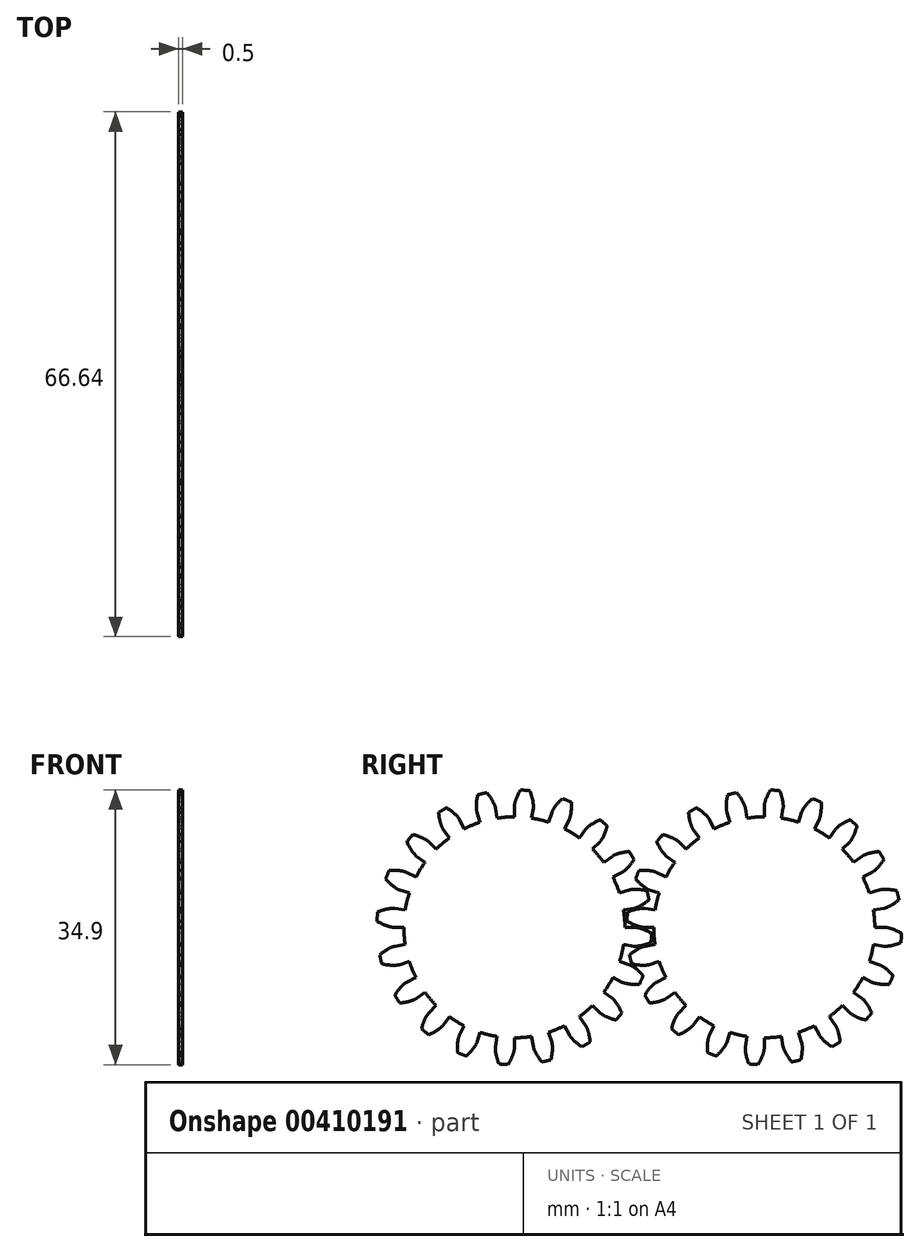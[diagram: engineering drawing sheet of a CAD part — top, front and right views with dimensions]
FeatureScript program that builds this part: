
annotation { "Feature Type Name" : "Feature", "Feature Type Description" : "" }
export const myFeature = defineFeature(function(context is Context, id is Id, definition is map)
    precondition{}
    {
        {
            assignVariable(context, id + "F0", {"name" : "NumberTeeth", "anyValue" : 20});
        }
        {
            assignVariable(context, id + "F1", {"name" : "GearThickness", "anyValue" : .5});
        }
        {
            var Q0;
            Q0=qCreatedBy(makeId("Right.planeOp"),FACE);
            var sketch = newSketch(context, id + "F2", { "sketchPlane" : qUnion([Q0])});
            skCircle(sketch, "E0", {"center": v(0, 0) * mm, "radius": 14.04 * mm});
            skCircle(sketch, "E1", {"center": v(0, 0) * mm, "radius": 15.37 * mm, "construction": true});
            skCircle(sketch, "E2", {"center": v(0, 0) * mm, "radius": 15.88 * mm, "construction": true});
            skCircle(sketch, "E3", {"center": v(0, 0) * mm, "radius": 17.46 * mm});
            skLineSegment(sketch, "E4", {"start": v(0, 0) * mm, "end": v(-15.37, 0) * mm, "construction": true});
            skLineSegment(sketch, "E5.1.0", {"start": v(0, 0) * mm, "end": v(-15.35, 0.77) * mm, "construction": true});
            skLineSegment(sketch, "E5.2.0", {"start": v(0, 0) * mm, "end": v(-15.3, 1.53) * mm, "construction": true});
            skLineSegment(sketch, "E5.3.0", {"start": v(0, 0) * mm, "end": v(-15.2, 2.3) * mm, "construction": true});
            skLineSegment(sketch, "E5.4.0", {"start": v(0, 0) * mm, "end": v(-15.06, 3.05) * mm, "construction": true});
            skLineSegment(sketch, "E5.5.0", {"start": v(0, 0) * mm, "end": v(-14.9, 3.8) * mm, "construction": true});
            skLineSegment(sketch, "E5.6.0", {"start": v(0, 0) * mm, "end": v(-14.68, 4.54) * mm, "construction": true});
            skLineSegment(sketch, "E5.7.0", {"start": v(0, 0) * mm, "end": v(-14.44, 5.27) * mm, "construction": true});
            skLineSegment(sketch, "E5.8.0", {"start": v(0, 0) * mm, "end": v(-14.16, 5.99) * mm, "construction": true});
            skLineSegment(sketch, "E5.9.0", {"start": v(0, 0) * mm, "end": v(-13.84, 6.69) * mm, "construction": true});
            skLineSegment(sketch, "E5.10.0", {"start": v(0, 0) * mm, "end": v(-13.49, 7.37) * mm, "construction": true});
            skLineSegment(sketch, "E5.11.0", {"start": v(0, 0) * mm, "end": v(-13.1, 8.03) * mm, "construction": true});
            skLineSegment(sketch, "E5.12.0", {"start": v(0, 0) * mm, "end": v(-12.68, 8.68) * mm, "construction": true});
            skLineSegment(sketch, "E5.13.0", {"start": v(0, 0) * mm, "end": v(-12.24, 9.3) * mm, "construction": true});
            skLineSegment(sketch, "E5.14.0", {"start": v(0, 0) * mm, "end": v(-11.76, 9.9) * mm, "construction": true});
            skLineSegment(sketch, "E5.anchor2", {"start": v(0, 0) * mm, "end": v(-11.76, 9.9) * mm, "construction": true});
            skLineSegment(sketch, "E6", {"start": v(-15.35, 0.77) * mm, "end": v(-15.39, 0) * mm, "construction": true});
            skLineSegment(sketch, "E7", {"start": v(-15.3, 1.53) * mm, "end": v(-15.45, 0) * mm, "construction": true});
            skLineSegment(sketch, "E8", {"start": v(-15.2, 2.3) * mm, "end": v(-15.54, 0.02) * mm, "construction": true});
            skLineSegment(sketch, "E9", {"start": v(-14.9, 3.8) * mm, "end": v(-15.84, 0.08) * mm, "construction": true});
            skLineSegment(sketch, "E10", {"start": v(-14.68, 4.54) * mm, "end": v(-16.05, 0.14) * mm, "construction": true});
            skLineSegment(sketch, "E11", {"start": v(-14.44, 5.27) * mm, "end": v(-16.28, 0.22) * mm, "construction": true});
            skLineSegment(sketch, "E12", {"start": v(-14.16, 5.99) * mm, "end": v(-16.55, 0.32) * mm, "construction": true});
            skLineSegment(sketch, "E13", {"start": v(-13.84, 6.69) * mm, "end": v(-16.85, 0.46) * mm, "construction": true});
            skLineSegment(sketch, "E14", {"start": v(-13.49, 7.37) * mm, "end": v(-17.17, 0.62) * mm, "construction": true});
            skLineSegment(sketch, "E15", {"start": v(-13.1, 8.03) * mm, "end": v(-17.52, 0.83) * mm, "construction": true});
            skLineSegment(sketch, "E16", {"start": v(-15.06, 3.05) * mm, "end": v(-15.67, 0.04) * mm, "construction": true});
            skLineSegment(sketch, "E17", {"start": v(-12.68, 8.68) * mm, "end": v(-17.9, 1.07) * mm, "construction": true});
            skLineSegment(sketch, "E18", {"start": v(-12.24, 9.3) * mm, "end": v(-18.28, 1.35) * mm, "construction": true});
            skLineSegment(sketch, "E19", {"start": v(-11.76, 9.9) * mm, "end": v(-18.69, 1.67) * mm, "construction": true});
            skLineSegment(sketch, "E20", {"start": v(0, 0) * mm, "end": v(-15.32, 1.2) * mm, "construction": true});
            skLineSegment(sketch, "E21", {"start": v(-14.04, 0) * mm, "end": v(-15.37, 0) * mm});
            skLineSegment(sketch, "E22.MirrorCS", {"start": v(-13.87, 2.2) * mm, "end": v(-15.18, 2.4) * mm});
            skFitSpline(sketch, "E23", {"points": [v(-15.37, 0) * mm, v(-15.39, 0) * mm, v(-15.45, 0) * mm, v(-15.54, 0.02) * mm, v(-15.67, 0.04) * mm, v(-15.84, 0.08) * mm, v(-16.05, 0.14) * mm, v(-16.28, 0.22) * mm, v(-16.55, 0.32) * mm, v(-16.85, 0.46) * mm, v(-17.17, 0.62) * mm, v(-17.52, 0.83) * mm, v(-17.9, 1.07) * mm, v(-18.28, 1.35) * mm, v(-18.69, 1.67) * mm], "startDerivative": vector(-0.82, 0) * mm, "endDerivative": vector(-1.2, 1) * mm});
            skLineSegment(sketch, "E24", {"start": v(-18.69, 1.67) * mm, "end": v(-19.04, 1.97) * mm, "construction": true});
            skFitSpline(sketch, "E25.MirrorCS", {"points": [v(-15.18, 2.4) * mm, v(-15.2, 2.4) * mm, v(-15.26, 2.41) * mm, v(-15.35, 2.41) * mm, v(-15.49, 2.41) * mm, v(-15.66, 2.4) * mm, v(-15.87, 2.37) * mm, v(-16.12, 2.33) * mm, v(-16.4, 2.27) * mm, v(-16.71, 2.18) * mm, v(-17.06, 2.07) * mm, v(-17.43, 1.92) * mm, v(-17.84, 1.74) * mm, v(-18.27, 1.53) * mm, v(-18.72, 1.27) * mm], "startDerivative": vector(-0.8, 0.13) * mm, "endDerivative": vector(-1.34, -0.8) * mm});
            skSolve(sketch);
        }
        {
            var Q0;
            {var subQ0=sQuery(id+"F2.wireOp",EDGE,"E0");var subQ27=makeQuery(id+"F2.imprint","INTERSECT",VERTEX,{"derivedFrom":[subQ0,sQuery(id+"F2.wireOp",EDGE,"10ea1024-8cf5-41f5-a75f-a634b86921f3.10.0")]});Q0=makeQuery(id+"F2.imprint","IMPRINT",FACE,{"disambiguationData":[TD([[makeQuery(id+"F2.imprint","IMPRINT",EDGE,{"disambiguationData":[TD([[subQ27,-1.0]])],"derivedFrom":subQ0}),1.0]])]});}
            var Q1;
            {var subQ0=sQuery(id+"F2.wireOp",EDGE,"10ea1024-8cf5-41f5-a75f-a634b86921f3.1.0");Q1=makeQuery(id+"F2.imprint","IMPRINT",FACE,{"disambiguationData":[TD([[makeQuery(id+"F2.imprint","IMPRINT",EDGE,{"derivedFrom":subQ0}),-1.0]])]});}
            var Q2;
            {var subQ7=sQuery(id+"F2.wireOp",EDGE,"10ea1024-8cf5-41f5-a75f-a634b86921f3.2.0");Q2=makeQuery(id+"F2.imprint","IMPRINT",FACE,{"disambiguationData":[TD([[makeQuery(id+"F2.imprint","IMPRINT",EDGE,{"derivedFrom":subQ7}),-1.0]])]});}
            var Q3;
            {var subQ8=sQuery(id+"F2.wireOp",EDGE,"10ea1024-8cf5-41f5-a75f-a634b86921f3.3.0");Q3=makeQuery(id+"F2.imprint","IMPRINT",FACE,{"disambiguationData":[TD([[makeQuery(id+"F2.imprint","IMPRINT",EDGE,{"derivedFrom":subQ8}),-1.0]])]});}
            var Q4;
            {var subQ2=sQuery(id+"F2.wireOp",EDGE,"10ea1024-8cf5-41f5-a75f-a634b86921f3.4.0");Q4=makeQuery(id+"F2.imprint","IMPRINT",FACE,{"disambiguationData":[TD([[makeQuery(id+"F2.imprint","IMPRINT",EDGE,{"derivedFrom":subQ2}),-1.0]])]});}
            var Q5;
            {var subQ8=sQuery(id+"F2.wireOp",EDGE,"10ea1024-8cf5-41f5-a75f-a634b86921f3.5.0");Q5=makeQuery(id+"F2.imprint","IMPRINT",FACE,{"disambiguationData":[TD([[makeQuery(id+"F2.imprint","IMPRINT",EDGE,{"derivedFrom":subQ8}),-1.0]])]});}
            var Q6;
            {var subQ3=sQuery(id+"F2.wireOp",EDGE,"10ea1024-8cf5-41f5-a75f-a634b86921f3.6.0");Q6=makeQuery(id+"F2.imprint","IMPRINT",FACE,{"disambiguationData":[TD([[makeQuery(id+"F2.imprint","IMPRINT",EDGE,{"derivedFrom":subQ3}),-1.0]])]});}
            var Q7;
            {var subQ0=sQuery(id+"F2.wireOp",EDGE,"10ea1024-8cf5-41f5-a75f-a634b86921f3.7.0");Q7=makeQuery(id+"F2.imprint","IMPRINT",FACE,{"disambiguationData":[TD([[makeQuery(id+"F2.imprint","IMPRINT",EDGE,{"derivedFrom":subQ0}),-1.0]])]});}
            var Q8;
            {var subQ5=sQuery(id+"F2.wireOp",EDGE,"10ea1024-8cf5-41f5-a75f-a634b86921f3.8.0");Q8=makeQuery(id+"F2.imprint","IMPRINT",FACE,{"disambiguationData":[TD([[makeQuery(id+"F2.imprint","IMPRINT",EDGE,{"derivedFrom":subQ5}),-1.0]])]});}
            var Q9;
            {var subQ1=sQuery(id+"F2.wireOp",EDGE,"10ea1024-8cf5-41f5-a75f-a634b86921f3.9.0");Q9=makeQuery(id+"F2.imprint","IMPRINT",FACE,{"disambiguationData":[TD([[makeQuery(id+"F2.imprint","IMPRINT",EDGE,{"derivedFrom":subQ1}),-1.0]])]});}
            var Q10;
            {var subQ5=sQuery(id+"F2.wireOp",EDGE,"10ea1024-8cf5-41f5-a75f-a634b86921f3.10.0");Q10=makeQuery(id+"F2.imprint","IMPRINT",FACE,{"disambiguationData":[TD([[makeQuery(id+"F2.imprint","IMPRINT",EDGE,{"derivedFrom":subQ5}),-1.0]])]});}
            var Q11;
            {var subQ8=sQuery(id+"F2.wireOp",EDGE,"10ea1024-8cf5-41f5-a75f-a634b86921f3.11.0");Q11=makeQuery(id+"F2.imprint","IMPRINT",FACE,{"disambiguationData":[TD([[makeQuery(id+"F2.imprint","IMPRINT",EDGE,{"derivedFrom":subQ8}),-1.0]])]});}
            var Q12;
            {var subQ2=sQuery(id+"F2.wireOp",EDGE,"10ea1024-8cf5-41f5-a75f-a634b86921f3.12.0");Q12=makeQuery(id+"F2.imprint","IMPRINT",FACE,{"disambiguationData":[TD([[makeQuery(id+"F2.imprint","IMPRINT",EDGE,{"derivedFrom":subQ2}),-1.0]])]});}
            var Q13;
            {var subQ3=sQuery(id+"F2.wireOp",EDGE,"10ea1024-8cf5-41f5-a75f-a634b86921f3.13.0");Q13=makeQuery(id+"F2.imprint","IMPRINT",FACE,{"disambiguationData":[TD([[makeQuery(id+"F2.imprint","IMPRINT",EDGE,{"derivedFrom":subQ3}),-1.0]])]});}
            var Q14;
            {var subQ0=sQuery(id+"F2.wireOp",EDGE,"10ea1024-8cf5-41f5-a75f-a634b86921f3.14.0");Q14=makeQuery(id+"F2.imprint","IMPRINT",FACE,{"disambiguationData":[TD([[makeQuery(id+"F2.imprint","IMPRINT",EDGE,{"derivedFrom":subQ0}),-1.0]])]});}
            var Q15;
            {var subQ6=sQuery(id+"F2.wireOp",EDGE,"10ea1024-8cf5-41f5-a75f-a634b86921f3.15.0");Q15=makeQuery(id+"F2.imprint","IMPRINT",FACE,{"disambiguationData":[TD([[makeQuery(id+"F2.imprint","IMPRINT",EDGE,{"derivedFrom":subQ6}),-1.0]])]});}
            var Q16;
            {var subQ5=sQuery(id+"F2.wireOp",EDGE,"10ea1024-8cf5-41f5-a75f-a634b86921f3.16.0");Q16=makeQuery(id+"F2.imprint","IMPRINT",FACE,{"disambiguationData":[TD([[makeQuery(id+"F2.imprint","IMPRINT",EDGE,{"derivedFrom":subQ5}),-1.0]])]});}
            var Q17;
            {var subQ7=sQuery(id+"F2.wireOp",EDGE,"10ea1024-8cf5-41f5-a75f-a634b86921f3.17.0");Q17=makeQuery(id+"F2.imprint","IMPRINT",FACE,{"disambiguationData":[TD([[makeQuery(id+"F2.imprint","IMPRINT",EDGE,{"derivedFrom":subQ7}),-1.0]])]});}
            var Q18;
            {var subQ5=sQuery(id+"F2.wireOp",EDGE,"10ea1024-8cf5-41f5-a75f-a634b86921f3.18.0");Q18=makeQuery(id+"F2.imprint","IMPRINT",FACE,{"disambiguationData":[TD([[makeQuery(id+"F2.imprint","IMPRINT",EDGE,{"derivedFrom":subQ5}),-1.0]])]});}
            var Q19;
            {var subQ8=sQuery(id+"F2.wireOp",EDGE,"10ea1024-8cf5-41f5-a75f-a634b86921f3.19.0");Q19=makeQuery(id+"F2.imprint","IMPRINT",FACE,{"disambiguationData":[TD([[makeQuery(id+"F2.imprint","IMPRINT",EDGE,{"derivedFrom":subQ8}),-1.0]])]});}
            var Q20;
            {var subQ8=sQuery(id+"F2.wireOp",EDGE,"E21");Q20=makeQuery(id+"F2.imprint","IMPRINT",FACE,{"disambiguationData":[TD([[makeQuery(id+"F2.imprint","IMPRINT",EDGE,{"derivedFrom":subQ8}),-1.0]])]});}
            extrude(context, id + "F3", {"entities" : qUnion([Q0, Q1, Q2, Q3, Q4, Q5, Q6, Q7, Q8, Q9, Q10, Q11, Q12, Q13, Q14, Q15, Q16, Q17, Q18, Q19, Q20]), "depth" : (getVariable(context, 'GearThickness')) * mm});
        }
        {
            var Q0;
            Q0=makeQuery(id+"F3.opExtrude","SWEPT_FACE",FACE,{"disambiguationData":[OSD([sQuery(id+"F2.wireOp",EDGE,"E25.MirrorCS")])]});
            var Q1;
            Q1=makeQuery(id+"F3.opExtrude","SWEPT_FACE",FACE,{"disambiguationData":[OSD([sQuery(id+"F2.wireOp",EDGE,"E23")])]});
            var Q2;
            Q2=makeQuery(id+"F3.opExtrude","SWEPT_FACE",FACE,{"disambiguationData":[OSD([sQuery(id+"F2.wireOp",EDGE,"E3")])]});
            var Q3;
            Q3=makeQuery(id+"F3.opExtrude","SWEPT_FACE",FACE,{"disambiguationData":[OSD([sQuery(id+"F2.wireOp",EDGE,"E22.MirrorCS")])]});
            var Q4;
            Q4=makeQuery(id+"F3.opExtrude","SWEPT_FACE",FACE,{"disambiguationData":[OSD([sQuery(id+"F2.wireOp",EDGE,"E21")])]});
            var Q5;
            Q5=makeQuery(id+"F3.opExtrude","SWEPT_FACE",FACE,{"disambiguationData":[OSD([sQuery(id+"F2.wireOp",EDGE,"E0")])]});
            circularPattern(context, id + "F4", {"faces" : qUnion([Q0, Q1, Q2, Q3, Q4]), "axis" : qUnion([Q5]), "angle" : 360 * degree, "instanceCount" : getVariable(context, 'NumberTeeth'), "equalSpace" : true, "patternType" : PatternType.FACE});
        }
        {
            var Q0;
            Q0=makeQuery(id+"F3.opExtrude","SWEPT_BODY",BODY,{"disambiguationData":[OSD([sQuery(id+"F2.wireOp",EDGE,"E0"),sQuery(id+"F2.wireOp",EDGE,"E3"),sQuery(id+"F2.wireOp",EDGE,"E21"),sQuery(id+"F2.wireOp",EDGE,"E22.MirrorCS"),sQuery(id+"F2.wireOp",EDGE,"E23"),sQuery(id+"F2.wireOp",EDGE,"E25.MirrorCS")])]});
            transform(context, id + "F5", {"entities" : qUnion([Q0]), "transformType" : TransformType.TRANSLATION_3D, "dx" : 0 * mm, "dy" : 33.33 * mm, "dz" : 0 * mm, "makeCopy" : true});
        }
        {
            var Q0;
            Q0=makeQuery(id+"F5.opPattern","COPY",BODY,{"derivedFrom":makeQuery(id+"F3.opExtrude","SWEPT_BODY",BODY,{"disambiguationData":[OSD([sQuery(id+"F2.wireOp",EDGE,"E0"),sQuery(id+"F2.wireOp",EDGE,"E3"),sQuery(id+"F2.wireOp",EDGE,"E21"),sQuery(id+"F2.wireOp",EDGE,"E22.MirrorCS"),sQuery(id+"F2.wireOp",EDGE,"E23"),sQuery(id+"F2.wireOp",EDGE,"E25.MirrorCS")])]}),"instanceName":"1"});
            transform(context, id + "F6", {"entities" : qUnion([Q0]), "transformType" : TransformType.TRANSLATION_3D, "dx" : 0 * mm, "dy" : -1.59 * mm, "dz" : 0 * mm, "makeCopy" : false});
        }
    });
